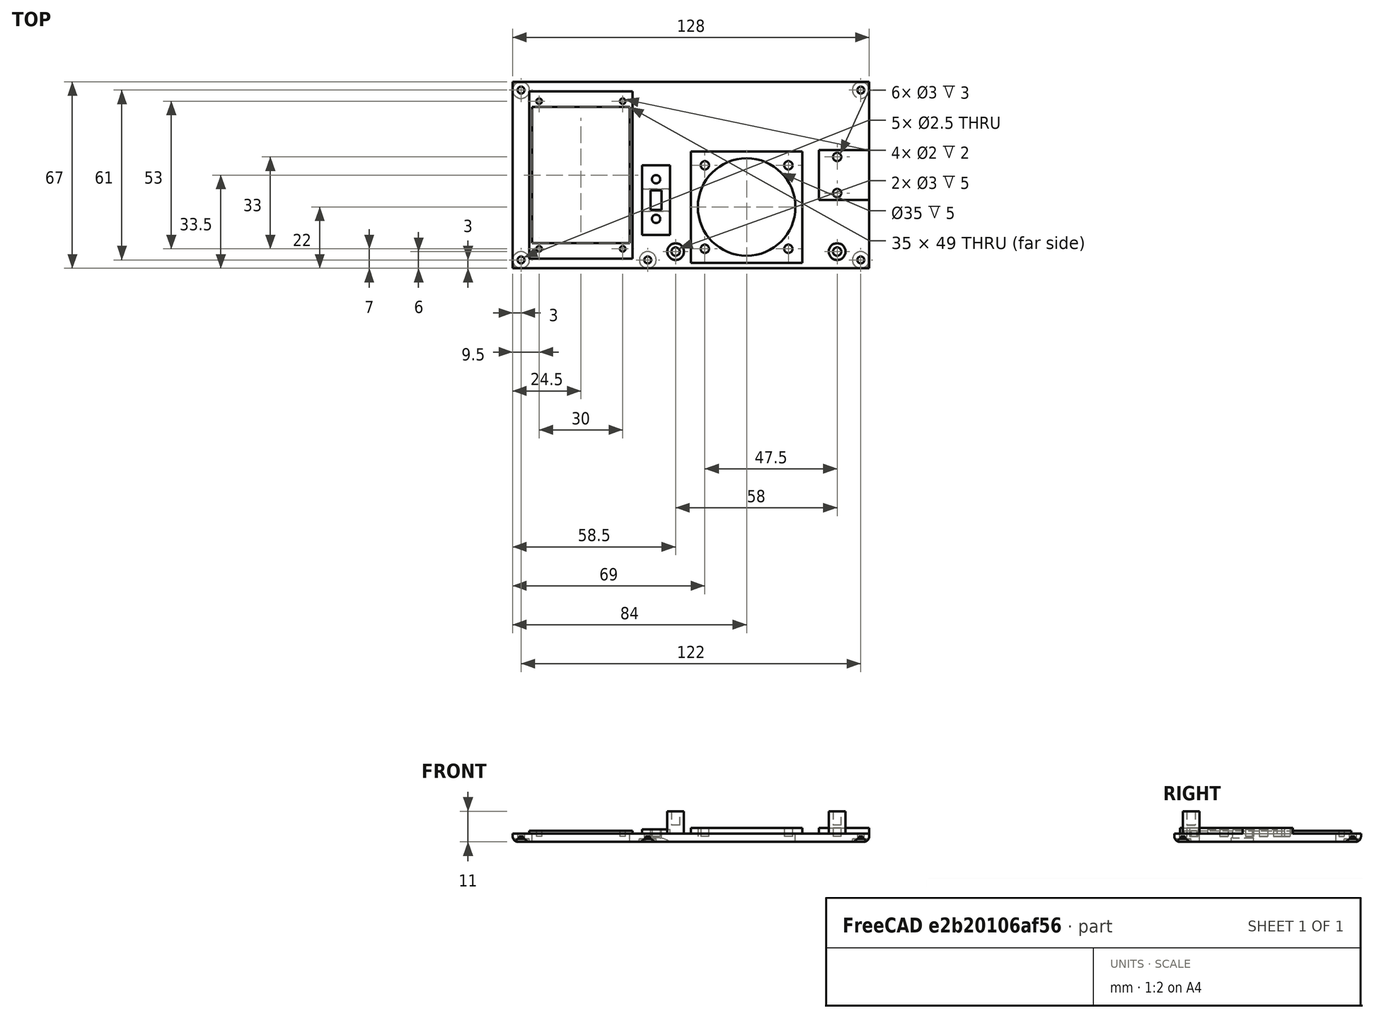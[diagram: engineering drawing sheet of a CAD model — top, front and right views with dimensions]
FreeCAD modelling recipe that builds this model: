
FCSTD DOCUMENT  (FreeCAD 1.0R39319 (Git))
Label: caseTopV3
License: All rights reserved
LicenseURL: https://en.wikipedia.org/wiki/All_rights_reserved
objects: PartDesign::SubtractiveCylinder×26, PartDesign::AdditiveBox×5, PartDesign::SubtractiveBox×2, PartDesign::AdditiveCylinder×2, PartDesign::Fillet×1, PartDesign::Body×1
note: 109 computed .brp shape members not serialized (recipe doc carries the construction recipe); baked Part::Feature solids carry a one-line shape summary decoded from their .brp

FEATURE [PartDesign::AdditiveBox] Box  label="base"
  AttacherType = Attacher::AttachEngine3D
  Height = 3
  Length = 128
  Refine = true
  Suppressed = false
  Width = 67
FEATURE [PartDesign::AdditiveBox] Box001  label="screenBase"
  AttacherType = Attacher::AttachEngine3D
  AttachmentOffset = pos=(6,3.5,0) rot=(0,0,1;0rad)
  AttachmentSupport = -> [Box]
  BaseFeature = -> Box
  Height = 1
  Length = 37
  MapMode = 5
  Placement = pos=(6,3.5,3) rot=(0,0,1;0rad)
  Refine = true
  Suppressed = false
  Width = 60
FEATURE [PartDesign::SubtractiveBox] Box002  label="screenCutout"
  AttacherType = Attacher::AttachEngine3D
  AttachmentOffset = pos=(1,5.5,-4) rot=(0,0,1;0rad)
  AttachmentSupport = -> [Box001]
  BaseFeature = -> Box001
  Height = 4
  Length = 35
  MapMode = 5
  Placement = pos=(7,9,0) rot=(0,0,1;0rad)
  Refine = true
  Suppressed = false
  Width = 49
FEATURE [PartDesign::AdditiveBox] Box004  label="clickwheelBase"
  AttacherType = Attacher::AttachEngine3D
  AttachmentOffset = pos=(20,-40,0) rot=(0,0,1;0rad)
  BaseFeature = -> Box002
  Height = 3
  Length = 40
  MapMode = 5
  Placement = pos=(64,2,2) rot=(0,0,1;0rad)
  Refine = true
  Suppressed = false
  Width = 40
FEATURE [PartDesign::SubtractiveCylinder] Cylinder  label="clickwheelCutout"
  Angle = 360
  AttacherType = Attacher::AttachEngine3D
  AttachmentOffset = pos=(20,20,-5) rot=(0,0,1;0rad)
  AttachmentSupport = -> [Box004]
  BaseFeature = -> Box004
  FirstAngle = 0
  Height = 5
  MapMode = 5
  Placement = pos=(84,22,0) rot=(0,0,1;0rad)
  Radius = 17.5
  Refine = true
  SecondAngle = 0
  Suppressed = false
FEATURE [PartDesign::AdditiveBox] Box005  label="chargingBase"
  AttacherType = Attacher::AttachEngine3D
  AttachmentOffset = pos=(9.5,19,0) rot=(0,0,1;0rad)
  BaseFeature = -> Cylinder
  Height = 2
  Length = 18
  MapMode = 5
  Placement = pos=(110,24.5,3) rot=(0,0,1;0rad)
  Refine = true
  Suppressed = false
  Width = 18
FEATURE [PartDesign::AdditiveCylinder] Cylinder007
  Angle = 360
  AttacherType = Attacher::AttachEngine3D
  AttachmentOffset = pos=(0,-35,0) rot=(0,0,1;0rad)
  BaseFeature = -> Box005
  FirstAngle = 0
  Height = 8
  MapMode = 5
  Placement = pos=(116.5,6,3) rot=(0,0,1;0rad)
  Radius = 3
  Refine = true
  SecondAngle = 0
  Suppressed = false
FEATURE [PartDesign::SubtractiveCylinder] Cylinder008
  Angle = 360
  AttacherType = Attacher::AttachEngine3D
  AttachmentOffset = pos=(0,0,-5) rot=(0,0,1;0rad)
  AttachmentSupport = -> [Cylinder007]
  BaseFeature = -> Cylinder007
  FirstAngle = 0
  Height = 6
  MapMode = 5
  Placement = pos=(116.5,6,6) rot=(0,0,1;0rad)
  Radius = 1.5
  Refine = true
  SecondAngle = 0
  Suppressed = false
FEATURE [PartDesign::AdditiveCylinder] Cylinder009
  Angle = 360
  AttacherType = Attacher::AttachEngine3D
  AttachmentOffset = pos=(-58,0,0) rot=(0,0,1;0rad)
  AttachmentSupport = -> [Cylinder008]
  BaseFeature = -> Cylinder008
  FirstAngle = 0
  Height = 8
  MapMode = 5
  Placement = pos=(58.5,6,3) rot=(0,0,1;0rad)
  Radius = 3
  Refine = true
  SecondAngle = 0
  Suppressed = false
FEATURE [PartDesign::SubtractiveCylinder] Cylinder010
  Angle = 360
  AttacherType = Attacher::AttachEngine3D
  AttachmentOffset = pos=(0,0,-5) rot=(0,0,1;0rad)
  AttachmentSupport = -> [Cylinder009]
  BaseFeature = -> Cylinder009
  FirstAngle = 0
  Height = 5
  MapMode = 5
  Placement = pos=(58.5,6,6) rot=(0,0,1;0rad)
  Radius = 1.5
  Refine = true
  SecondAngle = 0
  Suppressed = false
FEATURE [PartDesign::AdditiveBox] Box006  label="holdSwitchBase"
  AttacherType = Attacher::AttachEngine3D
  AttachmentOffset = pos=(-12,6,0) rot=(0,0,1;0rad)
  AttachmentSupport = -> [Cylinder010]
  BaseFeature = -> Cylinder010
  Height = 1.5
  Length = 10
  MapMode = 5
  Placement = pos=(46.5,12,3) rot=(0,0,1;0rad)
  Refine = true
  Suppressed = false
  Width = 25
FEATURE [PartDesign::SubtractiveBox] Box007  label="holdSwitchCutout"
  AttacherType = Attacher::AttachEngine3D
  AttachmentOffset = pos=(3,9,-5) rot=(0,0,1;0rad)
  AttachmentSupport = -> [Box006]
  BaseFeature = -> Box006
  Height = 6
  Length = 4
  MapMode = 5
  Placement = pos=(49.5,21,-0.5) rot=(0,0,1;0rad)
  Refine = true
  Suppressed = false
  Width = 7
FEATURE [PartDesign::SubtractiveCylinder] Cylinder011  label="holdSwitchLeftScrew"
  Angle = 360
  AttacherType = Attacher::AttachEngine3D
  AttachmentOffset = pos=(2,-3.25,-2.5) rot=(0,0,1;0rad)
  AttachmentSupport = -> [Box007]
  BaseFeature = -> Box007
  FirstAngle = 0
  Height = 2.5
  MapMode = 5
  Placement = pos=(51.5,17.75,2) rot=(0,0,1;0rad)
  Radius = 1.5
  Refine = true
  SecondAngle = 0
  Suppressed = false
FEATURE [PartDesign::SubtractiveCylinder] Cylinder012  label="holdSwitchRightScrew"
  Angle = 360
  AttacherType = Attacher::AttachEngine3D
  AttachmentOffset = pos=(0,14.25,-2.5) rot=(0,0,1;0rad)
  AttachmentSupport = -> [Cylinder011]
  BaseFeature = -> Cylinder011
  FirstAngle = 0
  Height = 2.5
  MapMode = 5
  Placement = pos=(51.5,32,2) rot=(0,0,1;0rad)
  Radius = 1.5
  Refine = true
  SecondAngle = 0
  Suppressed = false
FEATURE [PartDesign::SubtractiveCylinder] Cylinder013  label="screenScrewTopLeft"
  Angle = 360
  AttacherType = Attacher::AttachEngine3D
  AttachmentOffset = pos=(-42,-25,-2) rot=(0,0,1;0rad)
  AttachmentSupport = -> [Cylinder012]
  BaseFeature = -> Cylinder012
  FirstAngle = 0
  Height = 2
  MapMode = 5
  Placement = pos=(9.5,7,2) rot=(0,0,1;0rad)
  Radius = 1
  Refine = true
  SecondAngle = 0
  Suppressed = false
FEATURE [PartDesign::SubtractiveCylinder] Cylinder014  label="screenScrewTopRight"
  Angle = 360
  AttacherType = Attacher::AttachEngine3D
  AttachmentOffset = pos=(0,53,-2) rot=(0,0,1;0rad)
  AttachmentSupport = -> [Cylinder013]
  BaseFeature = -> Cylinder013
  FirstAngle = 0
  Height = 2
  MapMode = 5
  Placement = pos=(9.5,60,2) rot=(0,0,1;0rad)
  Radius = 1
  Refine = true
  SecondAngle = 0
  Suppressed = false
FEATURE [PartDesign::SubtractiveCylinder] Cylinder015  label="screenScrewBottomRight"
  Angle = 360
  AttacherType = Attacher::AttachEngine3D
  AttachmentOffset = pos=(30,0,-2) rot=(0,0,1;0rad)
  AttachmentSupport = -> [Cylinder014]
  BaseFeature = -> Cylinder014
  FirstAngle = 0
  Height = 2
  MapMode = 5
  Placement = pos=(39.5,60,2) rot=(0,0,1;0rad)
  Radius = 1
  Refine = true
  SecondAngle = 0
  Suppressed = false
FEATURE [PartDesign::SubtractiveCylinder] Cylinder016  label="screenScrewBottomLeft"
  Angle = 360
  AttacherType = Attacher::AttachEngine3D
  AttachmentOffset = pos=(0,-53,-2) rot=(0,0,1;0rad)
  AttachmentSupport = -> [Cylinder015]
  BaseFeature = -> Cylinder015
  FirstAngle = 0
  Height = 2
  MapMode = 5
  Placement = pos=(39.5,7,2) rot=(0,0,1;0rad)
  Radius = 1
  Refine = true
  SecondAngle = 0
  Suppressed = false
FEATURE [PartDesign::SubtractiveCylinder] Cylinder017  label="topLeftScrew"
  Angle = 360
  AttacherType = Attacher::AttachEngine3D
  AttachmentOffset = pos=(-36.5,-4,-3) rot=(0,0,1;0rad)
  AttachmentSupport = -> [Cylinder016]
  BaseFeature = -> Cylinder016
  FirstAngle = 0
  Height = 3
  MapMode = 5
  Placement = pos=(3,3,0) rot=(0,0,1;0rad)
  Radius = 1.25
  Refine = true
  SecondAngle = 0
  Suppressed = false
FEATURE [PartDesign::SubtractiveCylinder] Cylinder018  label="topRightScrew"
  Angle = 360
  AttacherType = Attacher::AttachEngine3D
  AttachmentOffset = pos=(0,61,-3) rot=(0,0,1;0rad)
  AttachmentSupport = -> [Cylinder017]
  BaseFeature = -> Cylinder017
  FirstAngle = 0
  Height = 3
  MapMode = 5
  Placement = pos=(3,64,0) rot=(0,0,1;0rad)
  Radius = 1.25
  Refine = true
  SecondAngle = 0
  Suppressed = false
FEATURE [PartDesign::SubtractiveCylinder] Cylinder019  label="bottomRightScrew"
  Angle = 360
  AttacherType = Attacher::AttachEngine3D
  AttachmentOffset = pos=(122,0,-3) rot=(0,0,1;0rad)
  AttachmentSupport = -> [Cylinder018]
  BaseFeature = -> Cylinder018
  FirstAngle = 0
  Height = 3
  MapMode = 5
  Placement = pos=(125,64,0) rot=(0,0,1;0rad)
  Radius = 1.25
  Refine = true
  SecondAngle = 0
  Suppressed = false
FEATURE [PartDesign::SubtractiveCylinder] Cylinder020  label="bottomLeftScrew"
  Angle = 360
  AttacherType = Attacher::AttachEngine3D
  AttachmentOffset = pos=(0,-61,-3) rot=(0,0,1;0rad)
  AttachmentSupport = -> [Cylinder019]
  BaseFeature = -> Cylinder019
  FirstAngle = 0
  Height = 3
  MapMode = 5
  Placement = pos=(125,3,0) rot=(0,0,1;0rad)
  Radius = 1.25
  Refine = true
  SecondAngle = 0
  Suppressed = false
FEATURE [PartDesign::SubtractiveCylinder] Cylinder021
  Angle = 360
  AttacherType = Attacher::AttachEngine3D
  AttachmentOffset = pos=(-56,4,-3) rot=(0,0,1;0rad)
  AttachmentSupport = -> [Cylinder020]
  BaseFeature = -> Cylinder020
  FirstAngle = 0
  Height = 3
  MapMode = 5
  Placement = pos=(69,7,2) rot=(0,0,1;0rad)
  Radius = 1.5
  Refine = true
  SecondAngle = 0
  Suppressed = false
FEATURE [PartDesign::SubtractiveCylinder] Cylinder022
  Angle = 360
  AttacherType = Attacher::AttachEngine3D
  AttachmentOffset = pos=(0,30,-3) rot=(0,0,1;0rad)
  AttachmentSupport = -> [Cylinder021]
  BaseFeature = -> Cylinder021
  FirstAngle = 0
  Height = 3
  MapMode = 5
  Placement = pos=(69,37,2) rot=(0,0,1;0rad)
  Radius = 1.5
  Refine = true
  SecondAngle = 0
  Suppressed = false
FEATURE [PartDesign::SubtractiveCylinder] Cylinder023
  Angle = 360
  AttacherType = Attacher::AttachEngine3D
  AttachmentOffset = pos=(30,0,-3) rot=(0,0,1;0rad)
  AttachmentSupport = -> [Cylinder022]
  BaseFeature = -> Cylinder022
  FirstAngle = 0
  Height = 3
  MapMode = 5
  Placement = pos=(99,37,2) rot=(0,0,1;0rad)
  Radius = 1.5
  Refine = true
  SecondAngle = 0
  Suppressed = false
FEATURE [PartDesign::SubtractiveCylinder] Cylinder024
  Angle = 360
  AttacherType = Attacher::AttachEngine3D
  AttachmentOffset = pos=(0,-30,-3) rot=(0,0,1;0rad)
  AttachmentSupport = -> [Cylinder023]
  BaseFeature = -> Cylinder023
  FirstAngle = 0
  Height = 3
  MapMode = 5
  Placement = pos=(99,7,2) rot=(0,0,1;0rad)
  Radius = 1.5
  Refine = true
  SecondAngle = 0
  Suppressed = false
FEATURE [PartDesign::SubtractiveCylinder] Cylinder025
  Angle = 360
  AttacherType = Attacher::AttachEngine3D
  AttachmentOffset = pos=(17.5,20,-3) rot=(0,0,1;0rad)
  AttachmentSupport = -> [Cylinder024]
  BaseFeature = -> Cylinder024
  FirstAngle = 0
  Height = 3
  MapMode = 5
  Placement = pos=(116.5,27,2) rot=(0,0,1;0rad)
  Radius = 1.5
  Refine = true
  SecondAngle = 0
  Suppressed = false
FEATURE [PartDesign::SubtractiveCylinder] Cylinder026
  Angle = 360
  AttacherType = Attacher::AttachEngine3D
  AttachmentOffset = pos=(0,13,-3) rot=(0,0,1;0rad)
  AttachmentSupport = -> [Cylinder025]
  BaseFeature = -> Cylinder025
  FirstAngle = 0
  Height = 3
  MapMode = 5
  Placement = pos=(116.5,40,2) rot=(0,0,1;0rad)
  Radius = 1.5
  Refine = true
  SecondAngle = 0
  Suppressed = false
FEATURE [PartDesign::SubtractiveCylinder] Cylinder027
  Angle = 360
  AttacherType = Attacher::AttachEngine3D
  AttachmentOffset = pos=(-65,19.5,7.5) rot=(1,0,0;1.5708rad)
  AttachmentSupport = -> [Cylinder026]
  BaseFeature = -> Cylinder026
  FirstAngle = 0
  Height = 8
  MapMode = 5
  Placement = pos=(51.5,20.5,-7.5) rot=(1,0,0;4.71239rad)
  Radius = 9
  Refine = true
  SecondAngle = 0
  Suppressed = false
FEATURE [PartDesign::SubtractiveCylinder] Cylinder028
  Angle = 360
  AttacherType = Attacher::AttachEngine3D
  AttachmentOffset = pos=(3,-17.5,-3) rot=(0,0,1;0rad)
  AttachmentSupport = -> [Cylinder027]
  BaseFeature = -> Cylinder027
  FirstAngle = 0
  Height = 3
  MapMode = 5
  Placement = pos=(48.5,3,3) rot=(0,1,0;3.14159rad)
  Radius = 1.25
  Refine = true
  SecondAngle = 0
  Suppressed = false
FEATURE [PartDesign::Fillet] Fillet
  Base = -> Cylinder028 [Edge33,Edge35,Edge5,Edge4]
  BaseFeature = -> Cylinder028
  Placement = pos=(48.5,3,3) rot=(0,1,0;3.14159rad)
  Radius = 2
  Refine = true
  SupportTransform = false
  Suppressed = false
  UseAllEdges = false
FEATURE [PartDesign::SubtractiveCylinder] Cylinder029
  Angle = 360
  AttacherType = Attacher::AttachEngine3D
  AttachmentOffset = pos=(0,0,-1) rot=(0,0,1;0rad)
  AttachmentSupport = -> [Fillet]
  BaseFeature = -> Fillet
  FirstAngle = 0
  Height = 1
  MapMode = 5
  Placement = pos=(48.5,3,1) rot=(0,1,0;3.14159rad)
  Radius = 3
  Refine = true
  SecondAngle = 0
  Suppressed = false
FEATURE [PartDesign::SubtractiveCylinder] Cylinder030
  Angle = 360
  AttacherType = Attacher::AttachEngine3D
  AttachmentOffset = pos=(45.5,0,-1) rot=(0,0,1;0rad)
  AttachmentSupport = -> [Cylinder029]
  BaseFeature = -> Cylinder029
  FirstAngle = 0
  Height = 1
  MapMode = 5
  Placement = pos=(3,3,1) rot=(0,1,0;3.14159rad)
  Radius = 3
  Refine = true
  SecondAngle = 0
  Suppressed = false
FEATURE [PartDesign::SubtractiveCylinder] Cylinder031
  Angle = 360
  AttacherType = Attacher::AttachEngine3D
  AttachmentOffset = pos=(0,61,-1) rot=(0,0,1;0rad)
  AttachmentSupport = -> [Cylinder030]
  BaseFeature = -> Cylinder030
  FirstAngle = 0
  Height = 1
  MapMode = 5
  Placement = pos=(3,64,1) rot=(0,1,0;3.14159rad)
  Radius = 3
  Refine = true
  SecondAngle = 0
  Suppressed = false
FEATURE [PartDesign::SubtractiveCylinder] Cylinder032
  Angle = 360
  AttacherType = Attacher::AttachEngine3D
  AttachmentOffset = pos=(-122,0,-1) rot=(0,0,1;0rad)
  AttachmentSupport = -> [Cylinder031]
  BaseFeature = -> Cylinder031
  FirstAngle = 0
  Height = 1
  MapMode = 5
  Placement = pos=(125,64,1) rot=(0,1,0;3.14159rad)
  Radius = 3
  Refine = true
  SecondAngle = 0
  Suppressed = false
FEATURE [PartDesign::SubtractiveCylinder] Cylinder033
  Angle = 360
  AttacherType = Attacher::AttachEngine3D
  AttachmentOffset = pos=(0,-61,-1) rot=(0,0,1;0rad)
  AttachmentSupport = -> [Cylinder032]
  BaseFeature = -> Cylinder032
  FirstAngle = 0
  Height = 1
  MapMode = 5
  Placement = pos=(125,3,1) rot=(0,1,0;3.14159rad)
  Radius = 3
  Refine = true
  SecondAngle = 0
  Suppressed = false
FEATURE [PartDesign::Body] Body
  AllowCompound = false
  Group = -> [Box,Box001,Box002,Box004,Cylinder,Box005,Cylinder007,Cylinder008,Cylinder009,Cylinder010,Box006,Box007,Cylinder011,Cylinder012,Cylinder013,Cylinder014,Cylinder015,Cylinder016,Cylinder017,Cylinder018,Cylinder019,Cylinder020,Cylinder021,Cylinder022,Cylinder023,Cylinder024,Cylinder025,Cylinder026,Cylinder027,Cylinder028,Fillet,Cylinder029,Cylinder030,Cylinder031,Cylinder032,Cylinder033]
  Origin = -> Origin
  Tip = -> Cylinder033
